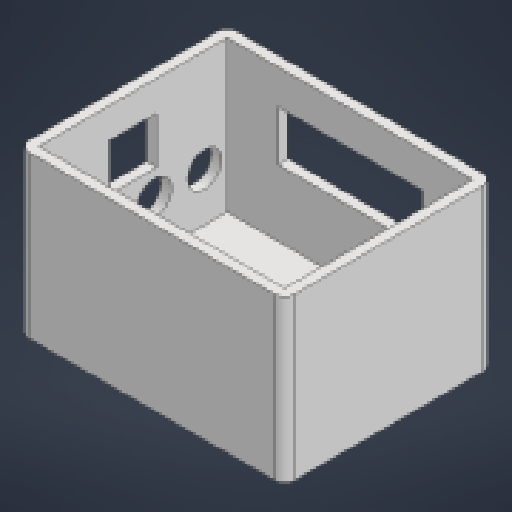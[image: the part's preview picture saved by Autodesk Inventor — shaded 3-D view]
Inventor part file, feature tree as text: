
AUTODESK INVENTOR PART (.ipt)
format: ipt  version: 2025.2 (Build 292293000, 293)  size: 186,368 bytes
history: native  units: mm
features: extrude x6, sketch x4, other x4, reference x3, fillet x1, mirror x1
ambient origin geometry x8: Origin, YZ Plane, XZ Plane, XY Plane, X Axis, Y Axis, Z Axis, Center Point
bodies: Solid1 (feature_tree)
feature tree (19):
  sketch  "Sketch1"  dims[d2=5.0mm d3=5.0mm d4=0.0mm]
  extrude  "Extrusion1"  Depth=5.0mm TaperAngle=0.0deg
  extrude  "Extrusion2"  Depth=57.0mm
  extrude  "Extrusion3"  Depth=3.5mm
  fillet  "Fillet1"  Radius=1.0mm
  extrude  "Extrusion4"  Depth=5.0mm
  extrude  "Extrusion5"  Depth=10.0mm
  mirror  "Mirror1"
  extrude  "Extrusion6"  Depth=10.0mm
  sketch  "Sketch2"  dims[d5=75.0mm d6=0.0mm d7=57.0mm]
  reference  "Reference1"
  reference  "Reference2"
  sketch  "Sketch3"  dims[d8=89.0mm d9=3.5mm d10=1.0mm]
  sketch  "Sketch4"  dims[d11=56.0mm d12=5.0mm d13=3.0mm d14=1.0mm d15=81.0mm d16=1.0mm d17=5.0mm d18=20.0mm d19=10.0mm d20=0.0mm d21=5.0mm d24=75.0mm d25=0.0mm d26=29.0mm d27=23.0mm d28=23.2mm d29=15.0mm d30=10.0mm d31=0.0mm d32=72.0mm d33=25.0mm d34=17.0mm d35=10.0mm d36=0.0mm]
  reference  "Reference5"
  other  "<userpath>\Desktop\Naks\Sklop.iam"
  other  "Sklop.iam"
  other  "ultrasonic:1"
  other  "display:1"
